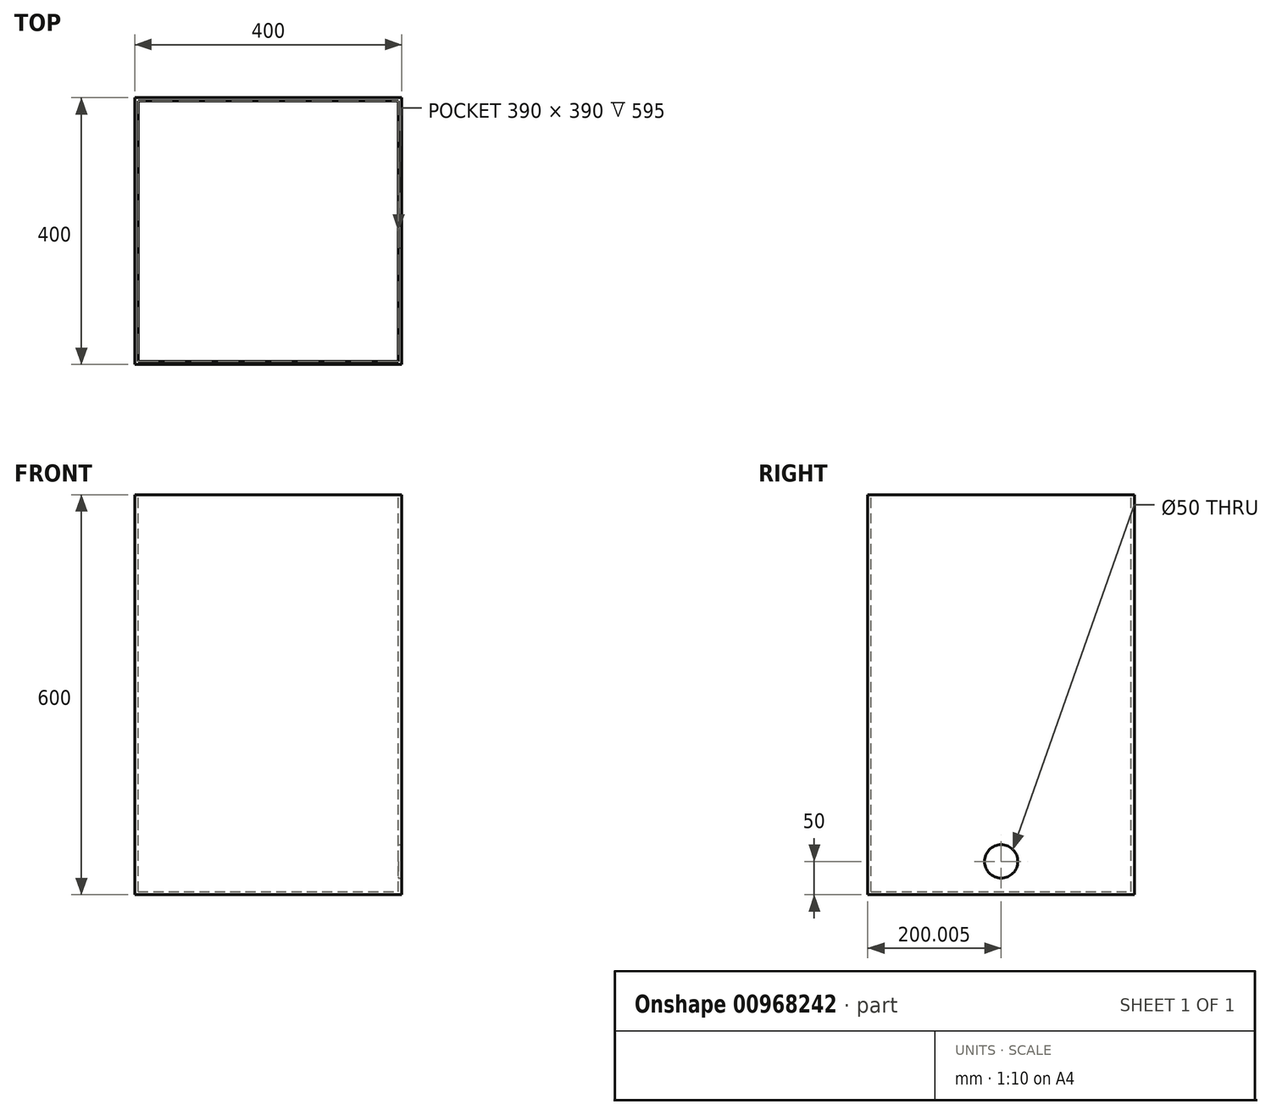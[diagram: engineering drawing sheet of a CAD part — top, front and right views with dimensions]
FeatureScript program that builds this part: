
annotation { "Feature Type Name" : "Feature", "Feature Type Description" : "" }
export const myFeature = defineFeature(function(context is Context, id is Id, definition is map)
    precondition{}
    {
        {
            var Q0;
            Q0=qCreatedBy(makeId("Top.planeOp"),FACE);
            var sketch = newSketch(context, id + "F0", { "sketchPlane" : qUnion([Q0])});
            skLineSegment(sketch, "E0", {"start": v(-132.52, -191.46) * mm, "end": v(-132.52, 208.54) * mm});
            skLineSegment(sketch, "E1", {"start": v(-132.52, 208.54) * mm, "end": v(267.48, 208.54) * mm});
            skLineSegment(sketch, "E2", {"start": v(-132.52, -191.46) * mm, "end": v(267.48, -191.46) * mm});
            skLineSegment(sketch, "E3", {"start": v(267.48, 208.54) * mm, "end": v(267.48, -191.46) * mm});
            skSolve(sketch);
        }
        {
            var Q0;
            Q0=makeQuery(id+"F0.imprint","IMPRINT",FACE,{"disambiguationData":[TD([[makeQuery(id+"F0.imprint","IMPRINT",EDGE,{"derivedFrom":sQuery(id+"F0.wireOp",EDGE,"E0")}),-1.0]])]});
            extrude(context, id + "F1", {"entities" : qUnion([Q0]), "oppositeDirection" : true, "depth" : 600 * mm, "offsetDistance" : 25 * mm});
        }
        {
            var Q0;
            Q0=makeQuery(id+"F1.opExtrude","CAP_FACE",FACE,{"disambiguationData":[OSD([sQuery(id+"F0.wireOp",EDGE,"E0"),sQuery(id+"F0.wireOp",EDGE,"E1"),sQuery(id+"F0.wireOp",EDGE,"E2"),sQuery(id+"F0.wireOp",EDGE,"E3")])],"isStart":true});
            shell(context, id + "F2", {"entities" : qUnion([Q0]), "thickness" : 5 * mm});
        }
        {
            var Q0;
            Q0=makeQuery(id+"F1.opExtrude","SWEPT_FACE",FACE,{"disambiguationData":[OSD([sQuery(id+"F0.wireOp",EDGE,"E3")])]});
            var sketch = newSketch(context, id + "F3", { "sketchPlane" : qUnion([Q0])});
            skCircle(sketch, "E4", {"center": v(8.54, -550) * mm, "radius": 25 * mm});
            skSolve(sketch);
        }
        {
            var Q0;
            Q0=qSketchRegion(id+"F3",true);
            extrude(context, id + "F4", {"entities" : qUnion([Q0]), "operationType" : NewBodyOperationType.REMOVE, "oppositeDirection" : true, "depth" : 30 * mm, "offsetDistance" : 25 * mm});
        }
    });
